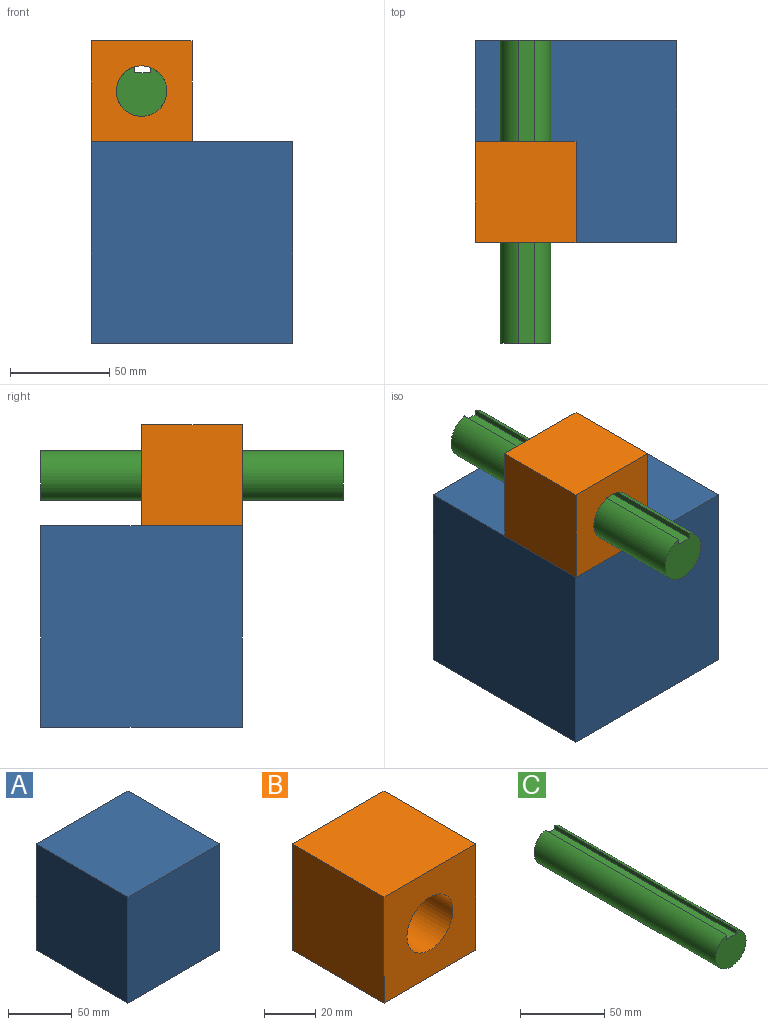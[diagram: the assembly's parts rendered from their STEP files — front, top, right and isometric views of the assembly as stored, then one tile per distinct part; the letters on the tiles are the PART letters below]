
ASSEMBLY  parts=3 mates=2
PART A: 6 faces, bbox 101.6x101.6x101.6 mm
  f0: plane 101.6x101.6mm, normal (0,0,1), area 10322.6mm2, adj f1,f3,f4,f5
  f1: plane 101.6x101.6mm, normal (-1,0,0), area 10322.6mm2, adj f0,f2,f4,f5
  f2: plane 101.6x101.6mm, normal (0,0,-1), area 10322.6mm2, adj f1,f3,f4,f5
  f3: plane 101.6x101.6mm, normal (1,0,0), area 10322.6mm2, adj f0,f2,f4,f5
  f4: plane 101.6x101.6mm, normal (0,-1,0), area 10322.6mm2, adj f0,f1,f2,f3
  f5: plane 101.6x101.6mm, normal (0,1,0), area 10322.6mm2, adj f0,f1,f2,f3
PART B: 7 faces, bbox 50.8x50.8x50.8 mm
  f0: plane 50.8x50.8mm, normal (-1,0,0), area 2580.6mm2, adj f1,f3,f4,f5
  f1: plane 50.8x50.8mm, normal (0,0,-1), area 2580.6mm2, adj f0,f2,f4,f5
  f2: plane 50.8x50.8mm, normal (1,0,0), area 2580.6mm2, adj f1,f3,f4,f5
  f3: plane 50.8x50.8mm, normal (0,0,1), area 2580.6mm2, adj f0,f2,f4,f5
  f4: plane 50.8x50.8mm, normal (0,-1,0), area 2073.9mm2, adj f0,f1,f2,f3,f6
  f5: plane 50.8x50.8mm, normal (0,1,0), area 2073.9mm2, adj f0,f1,f2,f3,f6
  f6: cylinder r=12.7mm len=50.8mm, axis (0,-1,0), area 4053.7mm2, adj f4,f5
PART C: 6 faces, bbox 25.4x152.4x24.9 mm
  f0: cylinder r=12.7mm len=152.4mm, axis (0,1,0), area 10950.7mm2, adj f1,f2,f3,f5
  f1: plane 25.4x24.93mm, normal (0,-1,0), area 480.4mm2, adj f0,f3,f4,f5
  f2: plane 25.4x24.93mm, normal (0,1,0), area 480.4mm2, adj f0,f3,f4,f5
  f3: plane 152.4x3.12mm, normal (1,0,0), area 474.9mm2, adj f0,f1,f2,f4
  f4: plane 152.4x7.81mm, normal (0,0,1), area 1189.7mm2, adj f1,f2,f3,f5
  f5: plane 152.4x2.81mm, normal (-1,0,0), area 428.3mm2, adj f0,f1,f2,f4
PLACE A t=(-105.38,48.96,0.21)mm fixed
PLACE B t=(-15.65,-1.84,17.59)mm
PLACE C t=(56.12,48.96,42.99)mm
MATE cylindrical C.f0 <-> B.f6  axis (0,1,0) through (9.75,-27.24,42.99)mm
MATE fastened A.f0 <-> B.f1  axis (0,0,1) through (35.15,-1.84,17.59)mm
